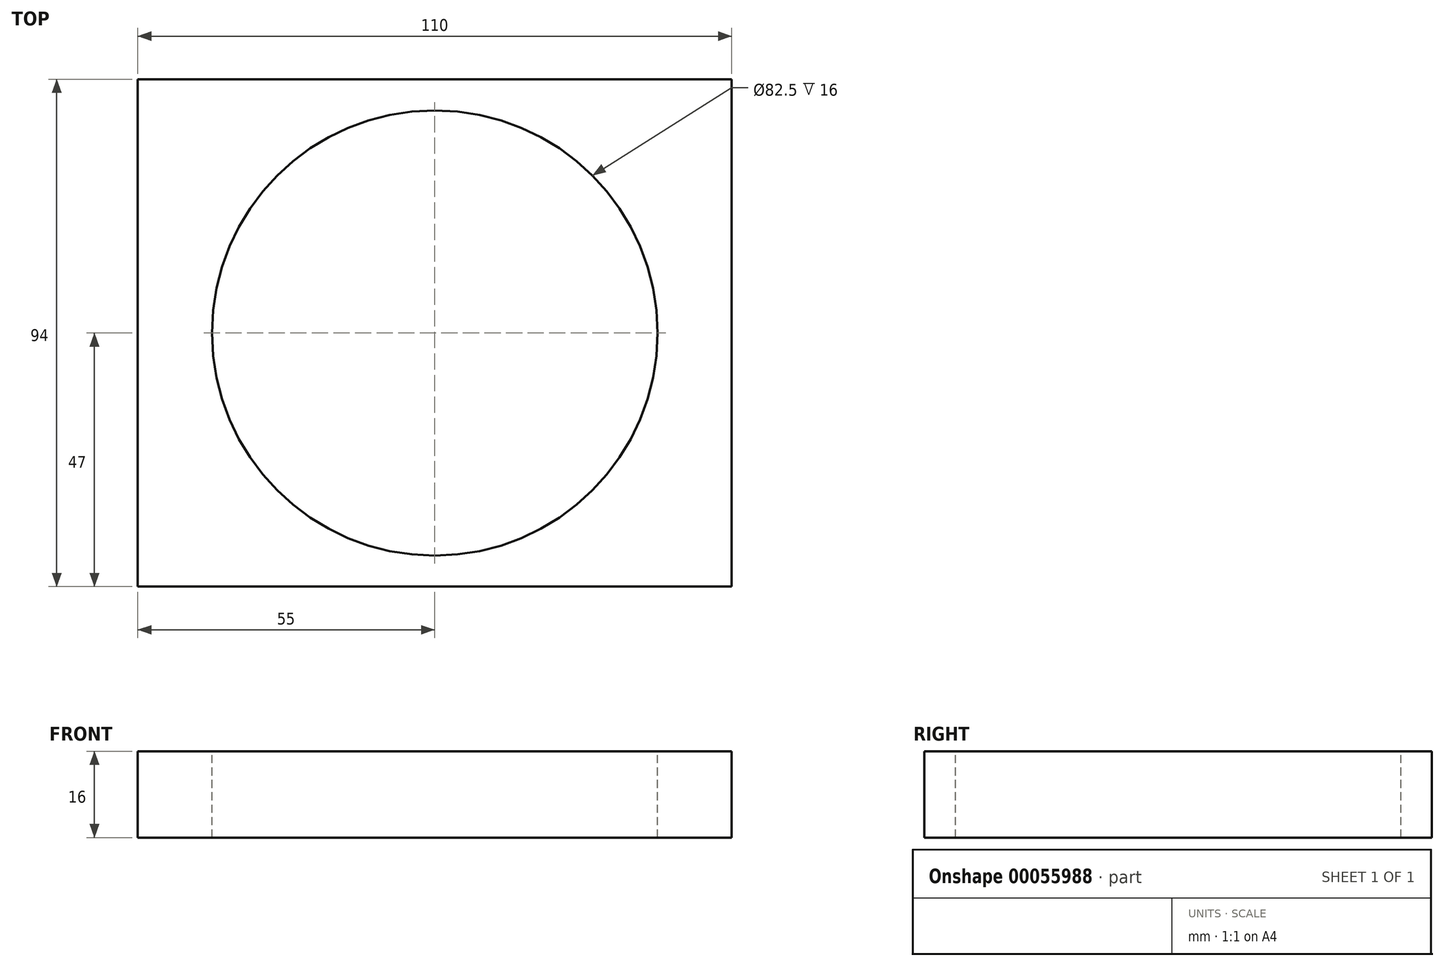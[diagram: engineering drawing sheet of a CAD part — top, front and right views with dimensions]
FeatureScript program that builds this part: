
annotation { "Feature Type Name" : "Feature", "Feature Type Description" : "" }
export const myFeature = defineFeature(function(context is Context, id is Id, definition is map)
    precondition{}
    {
        {
            var Q0;
            Q0=qCreatedBy(makeId("Top.planeOp"),FACE);
            var sketch = newSketch(context, id + "F0", { "sketchPlane" : qUnion([Q0])});
            skLineSegment(sketch, "E0.bottom", {"start": v(0, 0) * mm, "end": v(110, 0) * mm});
            skLineSegment(sketch, "E0.top", {"start": v(0, 94) * mm, "end": v(110, 94) * mm});
            skLineSegment(sketch, "E0.left", {"start": v(0, 0) * mm, "end": v(0, 94) * mm});
            skLineSegment(sketch, "E0.right", {"start": v(110, 0) * mm, "end": v(110, 94) * mm});
            skSolve(sketch);
        }
        {
            var Q0;
            Q0=makeQuery(id+"F0.imprint","IMPRINT",FACE,{"disambiguationData":[TD([[makeQuery(id+"F0.imprint","IMPRINT",EDGE,{"derivedFrom":sQuery(id+"F0.wireOp",EDGE,"E0.bottom")}),1.0]])]});
            extrude(context, id + "F1", {"entities" : qUnion([Q0]), "depth" : 16 * mm});
        }
        {
            var Q0;
            Q0=makeQuery(id+"F1.opExtrude","CAP_FACE",FACE,{"disambiguationData":[OSD([sQuery(id+"F0.wireOp",EDGE,"E0.bottom"),sQuery(id+"F0.wireOp",EDGE,"E0.top"),sQuery(id+"F0.wireOp",EDGE,"E0.left"),sQuery(id+"F0.wireOp",EDGE,"E0.right")])],"isStart":false});
            var sketch = newSketch(context, id + "F2", { "sketchPlane" : qUnion([Q0])});
            skLineSegment(sketch, "E1", {"start": v(0, 0) * mm, "end": v(0, 47) * mm});
            skLineSegment(sketch, "E2", {"start": v(110, 47) * mm, "end": v(0, 47) * mm});
            skLineSegment(sketch, "E3", {"start": v(55, 47) * mm, "end": v(55, 94) * mm});
            skSolve(sketch);
        }
        {
            var Q0;
            Q0=sQuery(id+"F2.wireOp",VERTEX,"E3.start");
            var Q1;
            Q1=makeQuery(id+"F1.opExtrude","SWEPT_BODY",BODY,{"disambiguationData":[OSD([sQuery(id+"F0.wireOp",EDGE,"E0.bottom"),sQuery(id+"F0.wireOp",EDGE,"E0.top"),sQuery(id+"F0.wireOp",EDGE,"E0.left"),sQuery(id+"F0.wireOp",EDGE,"E0.right")])]});
            hole(context, id + "F3", {"style" : HoleStyle.SIMPLE, "holeDiameter" : 82.5 * mm, "endStyle" : HoleEndStyle.THROUGH, "locations" : qUnion([Q0]), "scope" : qUnion([Q1])});
        }
    });
